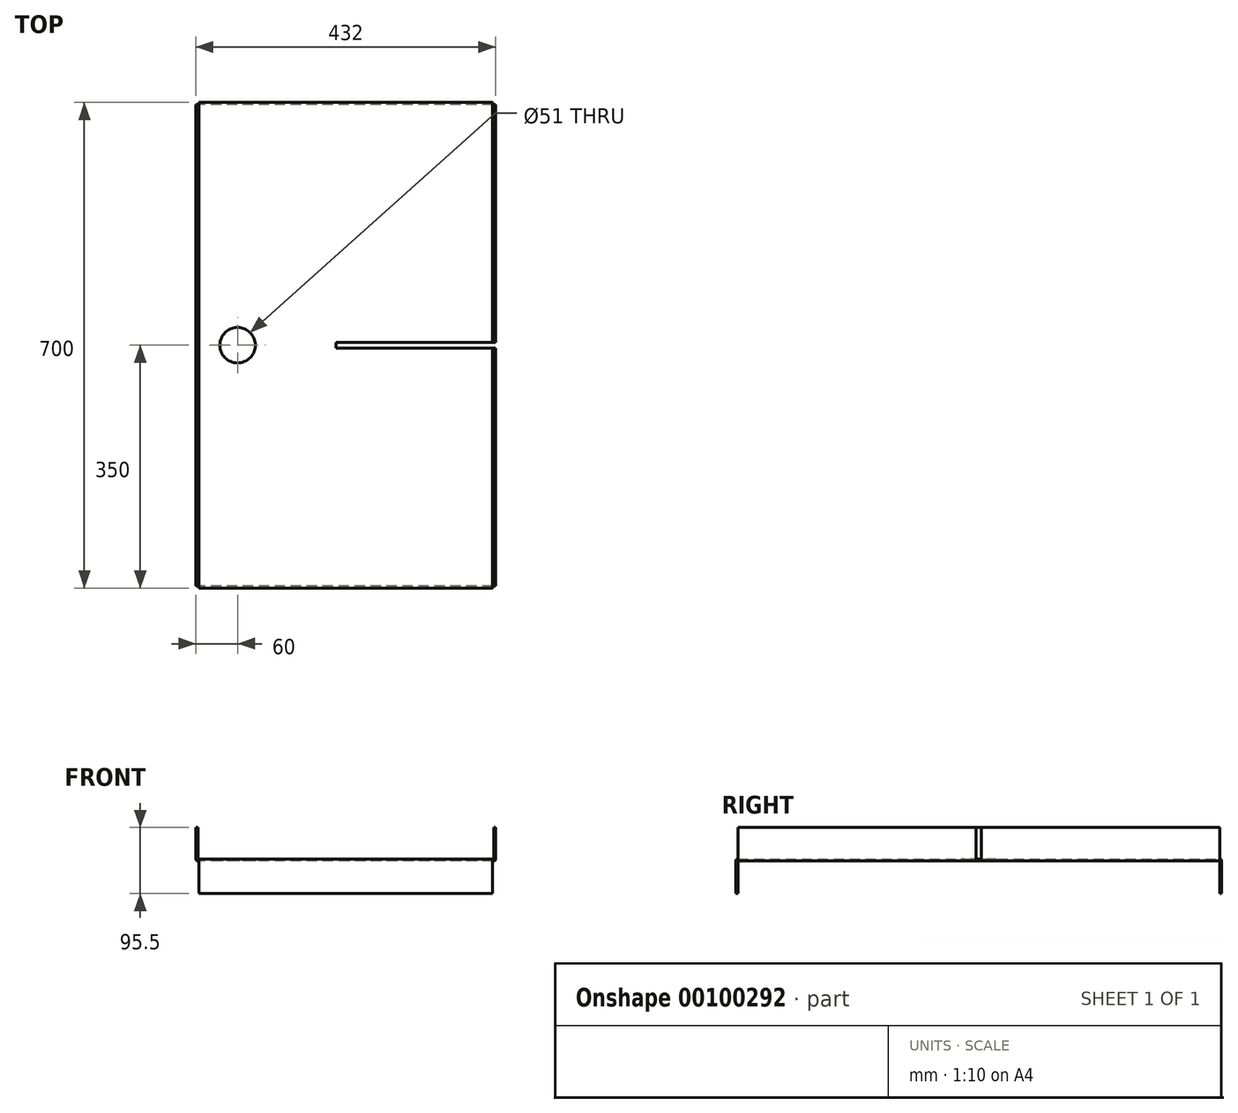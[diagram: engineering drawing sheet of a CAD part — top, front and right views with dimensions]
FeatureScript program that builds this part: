
annotation { "Feature Type Name" : "Feature", "Feature Type Description" : "" }
export const myFeature = defineFeature(function(context is Context, id is Id, definition is map)
    precondition{}
    {
        {
            var Q0;
            Q0=qCreatedBy(makeId("Right.planeOp"),FACE);
            var sketch = newSketch(context, id + "F0", { "sketchPlane" : qUnion([Q0])});
            skLineSegment(sketch, "E0", {"start": v(-350, 1.5) * mm, "end": v(-350, -45.5) * mm});
            skLineSegment(sketch, "E1", {"start": v(-345.5, 1.5) * mm, "end": v(345.5, 1.5) * mm});
            skLineSegment(sketch, "E2", {"start": v(350, -45.5) * mm, "end": v(350, 1.5) * mm});
            skLineSegment(sketch, "E3", {"start": v(-350, -45.5) * mm, "end": v(350, -45.5) * mm, "construction": true});
            skLineSegment(sketch, "E4", {"start": v(-350, -45.5) * mm, "end": v(-347, -45.5) * mm});
            skLineSegment(sketch, "E5", {"start": v(-347, 0) * mm, "end": v(-347, -45.5) * mm});
            skLineSegment(sketch, "E6", {"start": v(-347, 4.5) * mm, "end": v(347, 4.5) * mm});
            skLineSegment(sketch, "E7", {"start": v(347, -45.5) * mm, "end": v(347, 0) * mm});
            skLineSegment(sketch, "E8", {"start": v(347, -45.5) * mm, "end": v(350, -45.5) * mm});
            skPoint(sketch, "E9.visualSharp", {"position": v(-347, 1.5) * mm});
            skArc(sketch, "E9.filletArc", {"start": v(-345.5, 1.5) * mm, "mid": v(-346.56, 1.06) * mm, "end": v(-347, 0) * mm});
            skPoint(sketch, "E10.visualSharp", {"position": v(-350, 4.5) * mm});
            skArc(sketch, "E10.filletArc", {"start": v(-347, 4.5) * mm, "mid": v(-349.12, 3.62) * mm, "end": v(-350, 1.5) * mm});
            skPoint(sketch, "E11.visualSharp", {"position": v(350, 4.5) * mm});
            skArc(sketch, "E11.filletArc", {"start": v(350, 1.5) * mm, "mid": v(349.12, 3.62) * mm, "end": v(347, 4.5) * mm});
            skArc(sketch, "E12.filletArc", {"start": v(347, 0) * mm, "mid": v(346.56, 1.06) * mm, "end": v(345.5, 1.5) * mm});
            skSolve(sketch);
        }
        {
            var Q0;
            Q0=qSketchRegion(id+"F0",true);
            extrude(context, id + "F1", {"entities" : qUnion([Q0]), "depth" : 211.5 * mm, "hasSecondDirection" : true, "secondDirectionOppositeDirection" : true, "secondDirectionDepth" : 70 * mm});
        }
        {
            var Q0;
            Q0=qCreatedBy(makeId("Front.planeOp"),FACE);
            var sketch = newSketch(context, id + "F2", { "sketchPlane" : qUnion([Q0])});
            skLineSegment(sketch, "E13", {"start": v(213, 50) * mm, "end": v(216, 50) * mm});
            skLineSegment(sketch, "E14", {"start": v(216, 50) * mm, "end": v(216, 4.5) * mm});
            skLineSegment(sketch, "E15", {"start": v(213, 50) * mm, "end": v(213, 4.5) * mm});
            skArc(sketch, "E16.filletArc", {"start": v(211.5, 3) * mm, "mid": v(212.56, 3.44) * mm, "end": v(213, 4.5) * mm});
            skPoint(sketch, "E17.visualSharp", {"position": v(216, 0) * mm});
            skArc(sketch, "E17.filletArc", {"start": v(213, 1.5) * mm, "mid": v(215.12, 2.38) * mm, "end": v(216, 4.5) * mm});
            skLineSegment(sketch, "E18", {"start": v(211.5, 3) * mm, "end": v(211.5, 1.5) * mm});
            skLineSegment(sketch, "E19", {"start": v(213, 1.5) * mm, "end": v(211.5, 1.5) * mm});
            skSolve(sketch);
        }
        {
            var Q0;
            Q0=qSketchRegion(id+"F2",true);
            extrude(context, id + "F3", {"entities" : qUnion([Q0]), "operationType" : NewBodyOperationType.ADD, "depth" : 347 * mm, "hasSecondDirection" : true, "secondDirectionOppositeDirection" : true, "secondDirectionDepth" : 347 * mm});
        }
        {
            var Q0;
            Q0=makeQuery(id+"F1.opExtrude","SWEPT_BODY",BODY,{"disambiguationData":[OSD([sQuery(id+"F0.wireOp",EDGE,"E0"),sQuery(id+"F0.wireOp",EDGE,"E1"),sQuery(id+"F0.wireOp",EDGE,"E2"),sQuery(id+"F0.wireOp",EDGE,"E4"),sQuery(id+"F0.wireOp",EDGE,"E5"),sQuery(id+"F0.wireOp",EDGE,"E6"),sQuery(id+"F0.wireOp",EDGE,"E7"),sQuery(id+"F0.wireOp",EDGE,"E8"),sQuery(id+"F0.wireOp",EDGE,"E9.filletArc"),sQuery(id+"F0.wireOp",EDGE,"E10.filletArc"),sQuery(id+"F0.wireOp",EDGE,"E11.filletArc"),sQuery(id+"F0.wireOp",EDGE,"E12.filletArc")])]});
            var Q1;
            Q1=qCreatedBy(makeId("Right.planeOp"),FACE);
            mirror(context, id + "F4", {"operationType" : NewBodyOperationType.ADD, "entities" : qUnion([Q0]), "mirrorPlane" : qUnion([Q1])});
        }
        {
            var Q0;
            Q0=qCreatedBy(makeId("Top.planeOp"),FACE);
            var sketch = newSketch(context, id + "F5", { "sketchPlane" : qUnion([Q0])});
            skLineSegment(sketch, "E20.bottom", {"start": v(-14, -4) * mm, "end": v(219.84, -4) * mm});
            skLineSegment(sketch, "E20.top", {"start": v(-14, 4) * mm, "end": v(219.84, 4) * mm});
            skLineSegment(sketch, "E20.left", {"start": v(-14, -4) * mm, "end": v(-14, 4) * mm});
            skLineSegment(sketch, "E20.right", {"start": v(219.84, -4) * mm, "end": v(219.84, 4) * mm});
            skSolve(sketch);
        }
        {
            var Q0;
            Q0=makeQuery(id+"F5.imprint","IMPRINT",FACE,{"disambiguationData":[TD([[makeQuery(id+"F5.imprint","IMPRINT",EDGE,{"derivedFrom":sQuery(id+"F5.wireOp",EDGE,"E20.bottom")}),1.0]])]});
            extrude(context, id + "F6", {"entities" : qUnion([Q0]), "operationType" : NewBodyOperationType.REMOVE, "depth" : 80 * mm});
        }
        {
            var Q0;
            {var subQ0=makeQuery(id+"F3.boolean.opBoolean","MERGE",FACE,{"derivedFrom":[makeQuery(id+"F1.opExtrude","SWEPT_FACE",FACE,{"disambiguationData":[OSD([sQuery(id+"F0.wireOp",EDGE,"E1")])]}),makeQuery(id+"F3.opExtrude","SWEPT_FACE",FACE,{"disambiguationData":[OSD([sQuery(id+"F2.wireOp",EDGE,"E19")])]})]});Q0=makeQuery(id+"F4.boolean.opBoolean","MERGE",FACE,{"derivedFrom":[subQ0,makeQuery(id+"F4.opPattern","COPY",FACE,{"derivedFrom":subQ0,"instanceName":"1"})]});}
            var sketch = newSketch(context, id + "F7", { "sketchPlane" : qUnion([Q0])});
            skCircle(sketch, "E21", {"center": v(-156, 0) * mm, "radius": 25.5 * mm});
            skSolve(sketch);
        }
        {
            var Q0;
            Q0 = qSketchRegion(id + "F7", true);
            extrude(context, id + "F8", {"entities" : qUnion([Q0]), "operationType" : NewBodyOperationType.REMOVE, "endBound" : BoundingType.SYMMETRIC, "oppositeDirection" : true, "depth" : 25 * mm});
        }
    });
